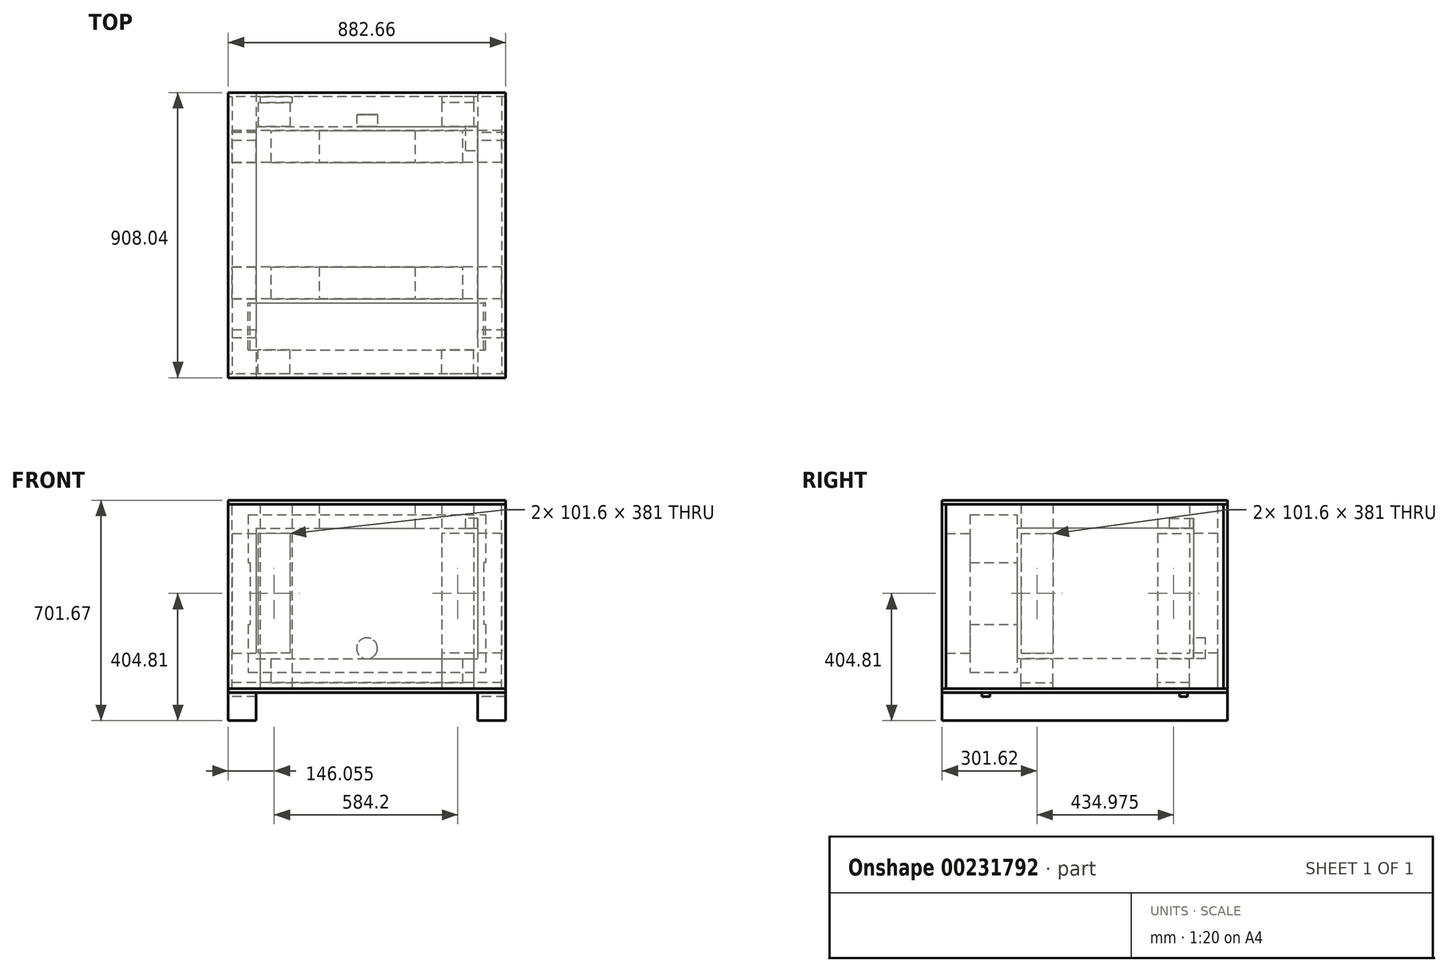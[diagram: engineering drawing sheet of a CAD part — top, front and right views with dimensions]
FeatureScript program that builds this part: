
annotation { "Feature Type Name" : "Feature", "Feature Type Description" : "" }
export const myFeature = defineFeature(function(context is Context, id is Id, definition is map)
    precondition{}
    {
        {
            var Q0;
            Q0=qCreatedBy(makeId("Front.planeOp"),FACE);
            var sketch = newSketch(context, id + "F0", { "sketchPlane" : qUnion([Q0])});
            skLineSegment(sketch, "E0.bottom", {"start": v(-377.83, 250.83) * mm, "end": v(377.83, 250.82) * mm});
            skLineSegment(sketch, "E0.top", {"start": v(-377.83, -250.82) * mm, "end": v(377.83, -250.83) * mm});
            skLineSegment(sketch, "E0.left", {"start": v(-377.82, 250.82) * mm, "end": v(-377.82, 98.43) * mm});
            skLineSegment(sketch, "E0.right", {"start": v(377.83, 250.83) * mm, "end": v(377.83, 98.43) * mm});
            skLineSegment(sketch, "E1.bottom", {"start": v(-377.82, 98.43) * mm, "end": v(-371.47, 98.43) * mm});
            skLineSegment(sketch, "E1.top", {"start": v(-377.83, -98.42) * mm, "end": v(-371.48, -98.42) * mm});
            skLineSegment(sketch, "E1.right", {"start": v(-371.48, 98.43) * mm, "end": v(-371.48, -98.42) * mm});
            skLineSegment(sketch, "E2", {"start": v(0, 250.82) * mm, "end": v(0, -250.82) * mm, "construction": true});
            skLineSegment(sketch, "E3.MirrorCS", {"start": v(377.82, 98.42) * mm, "end": v(371.47, 98.42) * mm});
            skLineSegment(sketch, "E4.MirrorCS", {"start": v(377.83, -98.43) * mm, "end": v(371.48, -98.43) * mm});
            skLineSegment(sketch, "E5.MirrorCS", {"start": v(371.47, 98.43) * mm, "end": v(371.48, -98.42) * mm});
            skLineSegment(sketch, "E6.trimOffspring", {"start": v(377.83, -98.42) * mm, "end": v(377.82, -250.83) * mm});
            skLineSegment(sketch, "E7.trimOffspring", {"start": v(-377.83, -98.42) * mm, "end": v(-377.83, -250.82) * mm});
            skLineSegment(sketch, "E8", {"start": v(371.48, 0) * mm, "end": v(-371.48, 0) * mm, "construction": true});
            skPoint(sketch, "E9", {"position": v(0, 0) * mm});
            skPoint(sketch, "E9.positionSnap0", {"position": v(0, 0) * mm});
            skSolve(sketch);
        }
        {
            var Q0;
            Q0=qSketchRegion(id+"F0",true);
            extrude(context, id + "F1", {"entities" : qUnion([Q0]), "depth" : 149.22 * mm});
        }
        {
            var Q0;
            Q0=makeQuery(id+"F1.opExtrude","CAP_FACE",FACE,{"disambiguationData":[OSD([sQuery(id+"F0.wireOp",EDGE,"E0.bottom"),sQuery(id+"F0.wireOp",EDGE,"E0.top"),sQuery(id+"F0.wireOp",EDGE,"E0.left"),sQuery(id+"F0.wireOp",EDGE,"E1.bottom"),sQuery(id+"F0.wireOp",EDGE,"E1.top"),sQuery(id+"F0.wireOp",EDGE,"E1.right"),sQuery(id+"F0.wireOp",EDGE,"E3.MirrorCS"),sQuery(id+"F0.wireOp",EDGE,"E4.MirrorCS"),sQuery(id+"F0.wireOp",EDGE,"E5.MirrorCS"),sQuery(id+"F0.wireOp",EDGE,"E0.right"),sQuery(id+"F0.wireOp",EDGE,"E7.trimOffspring"),sQuery(id+"F0.wireOp",EDGE,"E6.trimOffspring")])],"isStart":true});
            var sketch = newSketch(context, id + "F2", { "sketchPlane" : qUnion([Q0])});
            skPoint(sketch, "E10.0", {"position": v(377.82, 250.82) * mm});
            skPoint(sketch, "E11.0", {"position": v(-377.83, 250.83) * mm});
            skPoint(sketch, "E12.0", {"position": v(377.83, -250.82) * mm});
            skPoint(sketch, "E13.0", {"position": v(-377.82, -250.83) * mm});
            skLineSegment(sketch, "E14.bottom", {"start": v(352.43, 207.96) * mm, "end": v(-352.43, 207.96) * mm});
            skLineSegment(sketch, "E14.top", {"start": v(352.43, -207.96) * mm, "end": v(-352.43, -207.96) * mm});
            skLineSegment(sketch, "E14.left", {"start": v(352.43, 207.96) * mm, "end": v(352.43, -207.96) * mm});
            skLineSegment(sketch, "E14.right", {"start": v(-352.43, 207.96) * mm, "end": v(-352.43, -207.96) * mm});
            skPoint(sketch, "E14.middle", {"position": v(0, 0) * mm});
            skSolve(sketch);
        }
        {
            var Q0;
            Q0=qSketchRegion(id+"F2",true);
            extrude(context, id + "F3", {"entities" : qUnion([Q0]), "operationType" : NewBodyOperationType.ADD, "depth" : 561.98 * mm});
        }
        {
            var Q0;
            Q0=makeQuery(id+"F3.opExtrude","CAP_FACE",FACE,{"disambiguationData":[OSD([sQuery(id+"F2.wireOp",EDGE,"E14.bottom"),sQuery(id+"F2.wireOp",EDGE,"E14.top"),sQuery(id+"F2.wireOp",EDGE,"E14.left"),sQuery(id+"F2.wireOp",EDGE,"E14.right")])],"isStart":false});
            var sketch = newSketch(context, id + "F4", { "sketchPlane" : qUnion([Q0])});
            skLineSegment(sketch, "E15.bottom", {"start": v(-352.43, 207.96) * mm, "end": v(-314.33, 207.96) * mm});
            skLineSegment(sketch, "E15.top", {"start": v(-352.43, 239.71) * mm, "end": v(-314.33, 239.71) * mm});
            skLineSegment(sketch, "E15.left", {"start": v(-352.43, 207.96) * mm, "end": v(-352.43, 239.71) * mm});
            skLineSegment(sketch, "E15.right", {"start": v(-314.33, 207.96) * mm, "end": v(-314.33, 239.71) * mm});
            skSolve(sketch);
        }
        {
            var Q0;
            Q0=qSketchRegion(id+"F4",true);
            extrude(context, id + "F5", {"entities" : qUnion([Q0]), "operationType" : NewBodyOperationType.ADD, "oppositeDirection" : true, "depth" : 76.2 * mm});
        }
        {
            var Q0;
            Q0=makeQuery(id+"F5.boolean.opBoolean","MERGE",FACE,{"derivedFrom":[makeQuery(id+"F3.opExtrude","CAP_FACE",FACE,{"disambiguationData":[OSD([sQuery(id+"F2.wireOp",EDGE,"E14.bottom"),sQuery(id+"F2.wireOp",EDGE,"E14.top"),sQuery(id+"F2.wireOp",EDGE,"E14.left"),sQuery(id+"F2.wireOp",EDGE,"E14.right")])],"isStart":false}),makeQuery(id+"F5.opExtrude","CAP_FACE",FACE,{"disambiguationData":[OSD([sQuery(id+"F4.wireOp",EDGE,"E15.bottom"),sQuery(id+"F4.wireOp",EDGE,"E15.top"),sQuery(id+"F4.wireOp",EDGE,"E15.left"),sQuery(id+"F4.wireOp",EDGE,"E15.right")])],"isStart":true})]});
            var sketch = newSketch(context, id + "F6", { "sketchPlane" : qUnion([Q0])});
            skLineSegment(sketch, "E16", {"start": v(0, -207.96) * mm, "end": v(0, -174.63) * mm, "construction": true});
            skPoint(sketch, "E16.endSnap0", {"position": v(0, -207.96) * mm});
            skCircle(sketch, "E17", {"center": v(0, -174.63) * mm, "radius": 33.34 * mm});
            skSolve(sketch);
        }
        {
            var Q0;
            Q0=qSketchRegion(id+"F6",true);
            var Q1;
            Q1=qConstructionFilter(qBodyType(qCreatedBy(id+"F6",EDGE),BodyType.WIRE),ConstructionObject.NO);
            extrude(context, id + "F7", {"entities" : qUnion([Q0]), "operationType" : NewBodyOperationType.ADD, "surfaceEntities" : qUnion([Q1]), "depth" : 38.1 * mm});
        }
        {
            var Q0;
            Q0=makeQuery(id+"F3.opExtrude","SWEPT_FACE",FACE,{"disambiguationData":[OSD([sQuery(id+"F2.wireOp",EDGE,"E14.top")])]});
            var sketch = newSketch(context, id + "F8", { "sketchPlane" : qUnion([Q0])});
            skLineSegment(sketch, "E18.bottom", {"start": v(-304.8, -12.7) * mm, "end": v(304.8, -12.7) * mm});
            skLineSegment(sketch, "E18.top", {"start": v(-304.8, -114.3) * mm, "end": v(304.8, -114.3) * mm});
            skLineSegment(sketch, "E18.left", {"start": v(-304.8, -12.7) * mm, "end": v(-304.8, -114.3) * mm});
            skLineSegment(sketch, "E18.right", {"start": v(304.8, -12.7) * mm, "end": v(304.8, -114.3) * mm});
            skLineSegment(sketch, "E19.bottom", {"start": v(-304.8, -447.67) * mm, "end": v(304.8, -447.67) * mm});
            skLineSegment(sketch, "E19.top", {"start": v(-304.8, -549.27) * mm, "end": v(304.8, -549.27) * mm});
            skLineSegment(sketch, "E19.left", {"start": v(-304.8, -447.67) * mm, "end": v(-304.8, -549.27) * mm});
            skLineSegment(sketch, "E19.right", {"start": v(304.8, -447.67) * mm, "end": v(304.8, -549.27) * mm});
            skLineSegment(sketch, "E20", {"start": v(0, 0) * mm, "end": v(0, -561.98) * mm, "construction": true});
            skPoint(sketch, "E21", {"position": v(0, -114.3) * mm});
            skPoint(sketch, "E22", {"position": v(0, -447.67) * mm});
            skLineSegment(sketch, "E23.0", {"start": v(-377.83, 0) * mm, "end": v(377.82, 0) * mm, "construction": true});
            skLineSegment(sketch, "E24.0", {"start": v(0, -561.98) * mm, "end": v(352.43, -561.98) * mm, "construction": true});
            skLineSegment(sketch, "E25.0", {"start": v(-352.43, -561.98) * mm, "end": v(0, -561.98) * mm, "construction": true});
            skSolve(sketch);
        }
        {
            var Q0;
            Q0=qSketchRegion(id+"F8",true);
            extrude(context, id + "F9", {"entities" : qUnion([Q0]), "depth" : 76.2 * mm});
        }
        {
            var Q0;
            Q0=makeQuery(id+"F3.opExtrude","SWEPT_FACE",FACE,{"disambiguationData":[OSD([sQuery(id+"F2.wireOp",EDGE,"E14.bottom")])]});
            var sketch = newSketch(context, id + "F10", { "sketchPlane" : qUnion([Q0])});
            skLineSegment(sketch, "E26.0", {"start": v(-352.43, 561.98) * mm, "end": v(314.33, 561.98) * mm, "construction": true});
            skLineSegment(sketch, "E27.0", {"start": v(-377.82, 0) * mm, "end": v(377.83, 0) * mm, "construction": true});
            skPoint(sketch, "E28", {"position": v(0, 0) * mm});
            skLineSegment(sketch, "E29", {"start": v(0, 0) * mm, "end": v(0, 561.98) * mm, "construction": true});
            skLineSegment(sketch, "E30.bottom", {"start": v(-152.4, 549.27) * mm, "end": v(152.4, 549.27) * mm});
            skLineSegment(sketch, "E30.top", {"start": v(-152.4, 447.67) * mm, "end": v(152.4, 447.67) * mm});
            skLineSegment(sketch, "E30.left", {"start": v(-152.4, 549.27) * mm, "end": v(-152.4, 447.67) * mm});
            skLineSegment(sketch, "E30.right", {"start": v(152.4, 549.27) * mm, "end": v(152.4, 447.67) * mm});
            skLineSegment(sketch, "E31.bottom", {"start": v(-152.4, 114.3) * mm, "end": v(152.4, 114.3) * mm});
            skLineSegment(sketch, "E31.top", {"start": v(-152.4, 12.7) * mm, "end": v(152.4, 12.7) * mm});
            skLineSegment(sketch, "E31.left", {"start": v(-152.4, 114.3) * mm, "end": v(-152.4, 12.7) * mm});
            skLineSegment(sketch, "E31.right", {"start": v(152.4, 114.3) * mm, "end": v(152.4, 12.7) * mm});
            skPoint(sketch, "E32", {"position": v(0, 549.27) * mm});
            skPoint(sketch, "E33", {"position": v(0, 114.3) * mm});
            skSolve(sketch);
        }
        {
            var Q0;
            Q0=qSketchRegion(id+"F10",true);
            extrude(context, id + "F11", {"entities" : qUnion([Q0]), "depth" : 76.2 * mm});
        }
        {
            var Q0;
            Q0=makeQuery(id+"F5.boolean.opBoolean","MERGE",FACE,{"derivedFrom":[makeQuery(id+"F3.opExtrude","SWEPT_FACE",FACE,{"disambiguationData":[OSD([sQuery(id+"F2.wireOp",EDGE,"E14.right")])]}),makeQuery(id+"F5.opExtrude","SWEPT_FACE",FACE,{"disambiguationData":[OSD([sQuery(id+"F4.wireOp",EDGE,"E15.left")])]})]});
            var sketch = newSketch(context, id + "F12", { "sketchPlane" : qUnion([Q0])});
            skLineSegment(sketch, "E34.bottom", {"start": v(12.7, 190.5) * mm, "end": v(114.3, 190.5) * mm});
            skLineSegment(sketch, "E34.top", {"start": v(12.7, -190.5) * mm, "end": v(114.3, -190.5) * mm});
            skLineSegment(sketch, "E34.left", {"start": v(12.7, 190.5) * mm, "end": v(12.7, -190.5) * mm});
            skLineSegment(sketch, "E34.right", {"start": v(114.3, 190.5) * mm, "end": v(114.3, -190.5) * mm});
            skLineSegment(sketch, "E35.bottom", {"start": v(447.67, 190.5) * mm, "end": v(549.27, 190.5) * mm});
            skLineSegment(sketch, "E35.top", {"start": v(447.67, -190.5) * mm, "end": v(549.27, -190.5) * mm});
            skLineSegment(sketch, "E35.left", {"start": v(447.67, 190.5) * mm, "end": v(447.67, -190.5) * mm});
            skLineSegment(sketch, "E35.right", {"start": v(549.27, 190.5) * mm, "end": v(549.27, -190.5) * mm});
            skPoint(sketch, "E36", {"position": v(549.27, 0) * mm});
            skLineSegment(sketch, "E37.0", {"start": v(561.98, 207.96) * mm, "end": v(561.98, -207.96) * mm, "construction": true});
            skPoint(sketch, "E38", {"position": v(561.98, 0) * mm});
            skLineSegment(sketch, "E39", {"start": v(561.98, 0) * mm, "end": v(-342.54, 0) * mm, "construction": true});
            skSolve(sketch);
        }
        {
            var Q0;
            Q0=qSketchRegion(id+"F12",true);
            extrude(context, id + "F13", {"entities" : qUnion([Q0]), "depth" : 76.2 * mm});
        }
        {
            var Q0;
            Q0=makeQuery(id+"F9.opExtrude","CAP_FACE",FACE,{"disambiguationData":[OSD([sQuery(id+"F8.wireOp",EDGE,"E18.bottom"),sQuery(id+"F8.wireOp",EDGE,"E18.top"),sQuery(id+"F8.wireOp",EDGE,"E18.left"),sQuery(id+"F8.wireOp",EDGE,"E18.right")])],"isStart":false});
            var sketch = newSketch(context, id + "F14", { "sketchPlane" : qUnion([Q0])});
            skPoint(sketch, "E40.0", {"position": v(428.63, -12.7) * mm});
            skLineSegment(sketch, "E41.bottom", {"start": v(428.63, -12.7) * mm, "end": v(-428.63, -12.7) * mm});
            skLineSegment(sketch, "E41.top", {"start": v(428.63, -114.3) * mm, "end": v(-428.63, -114.3) * mm});
            skLineSegment(sketch, "E41.left", {"start": v(428.63, -12.7) * mm, "end": v(428.63, -114.3) * mm});
            skLineSegment(sketch, "E41.right", {"start": v(-428.63, -12.7) * mm, "end": v(-428.63, -114.3) * mm});
            skPoint(sketch, "E42.0", {"position": v(428.63, -549.27) * mm});
            skLineSegment(sketch, "E43.bottom", {"start": v(428.63, -549.27) * mm, "end": v(-428.63, -549.27) * mm});
            skLineSegment(sketch, "E43.top", {"start": v(428.63, -447.67) * mm, "end": v(-428.63, -447.68) * mm});
            skLineSegment(sketch, "E43.left", {"start": v(428.63, -549.27) * mm, "end": v(428.63, -447.67) * mm});
            skLineSegment(sketch, "E43.right", {"start": v(-428.63, -549.28) * mm, "end": v(-428.63, -447.68) * mm});
            skPoint(sketch, "E44.0", {"position": v(0, -447.67) * mm});
            skSolve(sketch);
        }
        {
            var Q0;
            Q0=qSketchRegion(id+"F14",true);
            extrude(context, id + "F15", {"entities" : qUnion([Q0]), "depth" : 19.05 * mm});
        }
        {
            var Q0;
            Q0=makeQuery(id+"F5.boolean.opBoolean","MERGE",FACE,{"derivedFrom":[makeQuery(id+"F3.opExtrude","CAP_FACE",FACE,{"disambiguationData":[OSD([sQuery(id+"F2.wireOp",EDGE,"E14.bottom"),sQuery(id+"F2.wireOp",EDGE,"E14.top"),sQuery(id+"F2.wireOp",EDGE,"E14.left"),sQuery(id+"F2.wireOp",EDGE,"E14.right")])],"isStart":false}),makeQuery(id+"F5.opExtrude","CAP_FACE",FACE,{"disambiguationData":[OSD([sQuery(id+"F4.wireOp",EDGE,"E15.bottom"),sQuery(id+"F4.wireOp",EDGE,"E15.top"),sQuery(id+"F4.wireOp",EDGE,"E15.left"),sQuery(id+"F4.wireOp",EDGE,"E15.right")])],"isStart":true})]});
            var sketch = newSketch(context, id + "F16", { "sketchPlane" : qUnion([Q0])});
            skLineSegment(sketch, "E45.0", {"start": v(0, -207.96) * mm, "end": v(-352.43, -207.96) * mm, "construction": true});
            skLineSegment(sketch, "E46.0", {"start": v(352.43, -207.96) * mm, "end": v(0, -207.96) * mm, "construction": true});
            skLineSegment(sketch, "E47.0", {"start": v(352.43, 207.96) * mm, "end": v(352.43, -207.96) * mm, "construction": true});
            skLineSegment(sketch, "E48.bottom", {"start": v(-339.73, 190.5) * mm, "end": v(-238.12, 190.5) * mm});
            skLineSegment(sketch, "E48.top", {"start": v(-339.73, -190.5) * mm, "end": v(-238.12, -190.5) * mm});
            skLineSegment(sketch, "E48.left", {"start": v(-339.73, 190.5) * mm, "end": v(-339.73, -190.5) * mm});
            skLineSegment(sketch, "E48.right", {"start": v(-238.13, 190.5) * mm, "end": v(-238.13, -190.5) * mm});
            skLineSegment(sketch, "E49.bottom", {"start": v(244.47, 190.5) * mm, "end": v(346.08, 190.5) * mm});
            skLineSegment(sketch, "E49.top", {"start": v(244.47, -190.5) * mm, "end": v(346.08, -190.5) * mm});
            skLineSegment(sketch, "E49.left", {"start": v(244.47, 190.5) * mm, "end": v(244.47, -190.5) * mm});
            skLineSegment(sketch, "E49.right", {"start": v(346.08, 190.5) * mm, "end": v(346.08, -190.5) * mm});
            skPoint(sketch, "E50", {"position": v(352.43, 0) * mm});
            skLineSegment(sketch, "E51", {"start": v(352.43, 0) * mm, "end": v(-564.26, 0) * mm, "construction": true});
            skPoint(sketch, "E52", {"position": v(346.08, 0) * mm});
            skSolve(sketch);
        }
        {
            var Q0;
            Q0=qSketchRegion(id+"F16",true);
            extrude(context, id + "F17", {"entities" : qUnion([Q0]), "depth" : 76.2 * mm});
        }
        {
            var Q0;
            Q0=makeQuery(id+"F3.opExtrude","SWEPT_FACE",FACE,{"disambiguationData":[OSD([sQuery(id+"F2.wireOp",EDGE,"E14.left")])]});
            cPlane(context, id + "F18", {"entities" : qUnion([Q0]), "cplaneType" : CPlaneType.OFFSET, "offset" : 352.42 * mm, "oppositeDirection" : true, "width" : 152.4 * mm, "height" : 152.4 * mm});
        }
        {
            var Q0;
            Q0=makeQuery(id+"F13.opExtrude","SWEPT_BODY",BODY,{"disambiguationData":[OSD([sQuery(id+"F12.wireOp",EDGE,"E35.bottom"),sQuery(id+"F12.wireOp",EDGE,"E35.top"),sQuery(id+"F12.wireOp",EDGE,"E35.left"),sQuery(id+"F12.wireOp",EDGE,"E35.right")])]});
            var Q1;
            Q1=makeQuery(id+"F13.opExtrude","SWEPT_BODY",BODY,{"disambiguationData":[OSD([sQuery(id+"F12.wireOp",EDGE,"E34.bottom"),sQuery(id+"F12.wireOp",EDGE,"E34.top"),sQuery(id+"F12.wireOp",EDGE,"E34.left"),sQuery(id+"F12.wireOp",EDGE,"E34.right")])]});
            var Q2;
            Q2=qCreatedBy(id+"F18.planeOp",FACE);
            mirror(context, id + "F19", {"operationType" : NewBodyOperationType.ADD, "entities" : qUnion([Q0, Q1]), "mirrorPlane" : qUnion([Q2])});
        }
        {
            var Q0;
            Q0=makeQuery(id+"F1.opExtrude","CAP_FACE",FACE,{"disambiguationData":[OSD([sQuery(id+"F0.wireOp",EDGE,"E0.bottom"),sQuery(id+"F0.wireOp",EDGE,"E0.top"),sQuery(id+"F0.wireOp",EDGE,"E0.left"),sQuery(id+"F0.wireOp",EDGE,"E1.bottom"),sQuery(id+"F0.wireOp",EDGE,"E1.top"),sQuery(id+"F0.wireOp",EDGE,"E1.right"),sQuery(id+"F0.wireOp",EDGE,"E3.MirrorCS"),sQuery(id+"F0.wireOp",EDGE,"E4.MirrorCS"),sQuery(id+"F0.wireOp",EDGE,"E5.MirrorCS"),sQuery(id+"F0.wireOp",EDGE,"E0.right"),sQuery(id+"F0.wireOp",EDGE,"E7.trimOffspring"),sQuery(id+"F0.wireOp",EDGE,"E6.trimOffspring")])],"isStart":false});
            cPlane(context, id + "F20", {"entities" : qUnion([Q0]), "cplaneType" : CPlaneType.OFFSET, "offset" : 355.6 * mm, "oppositeDirection" : true, "width" : 152.4 * mm, "height" : 152.4 * mm});
        }
        {
            var Q0;
            Q0=makeQuery(id+"F17.opExtrude","SWEPT_BODY",BODY,{"disambiguationData":[OSD([sQuery(id+"F16.wireOp",EDGE,"E49.bottom"),sQuery(id+"F16.wireOp",EDGE,"E49.top"),sQuery(id+"F16.wireOp",EDGE,"E49.left"),sQuery(id+"F16.wireOp",EDGE,"E49.right")])]});
            var Q1;
            Q1=makeQuery(id+"F17.opExtrude","SWEPT_BODY",BODY,{"disambiguationData":[OSD([sQuery(id+"F16.wireOp",EDGE,"E48.bottom"),sQuery(id+"F16.wireOp",EDGE,"E48.top"),sQuery(id+"F16.wireOp",EDGE,"E48.left"),sQuery(id+"F16.wireOp",EDGE,"E48.right")])]});
            var Q2;
            Q2=qCreatedBy(id+"F20.planeOp",FACE);
            mirror(context, id + "F21", {"operationType" : NewBodyOperationType.ADD, "entities" : qUnion([Q0, Q1]), "mirrorPlane" : qUnion([Q2])});
        }
        {
            var Q0;
            Q0=makeQuery(id+"F17.opExtrude","CAP_FACE",FACE,{"disambiguationData":[OSD([sQuery(id+"F16.wireOp",EDGE,"E48.bottom"),sQuery(id+"F16.wireOp",EDGE,"E48.top"),sQuery(id+"F16.wireOp",EDGE,"E48.left"),sQuery(id+"F16.wireOp",EDGE,"E48.right")])],"isStart":false});
            var sketch = newSketch(context, id + "F22", { "sketchPlane" : qUnion([Q0])});
            skLineSegment(sketch, "E53.bottom", {"start": v(-339.73, 284.16) * mm, "end": v(-238.13, 284.16) * mm});
            skLineSegment(sketch, "E53.top", {"start": v(-339.73, -303.21) * mm, "end": v(-238.12, -303.21) * mm});
            skLineSegment(sketch, "E53.left", {"start": v(-339.73, 284.16) * mm, "end": v(-339.73, -303.21) * mm});
            skLineSegment(sketch, "E53.right", {"start": v(-238.13, 284.16) * mm, "end": v(-238.13, -303.21) * mm});
            skLineSegment(sketch, "E54.0", {"start": v(152.4, 284.16) * mm, "end": v(-152.4, 284.16) * mm, "construction": true});
            skLineSegment(sketch, "E55.0", {"start": v(-428.63, -303.21) * mm, "end": v(428.63, -303.21) * mm, "construction": true});
            skSolve(sketch);
        }
        {
            var Q0;
            Q0=qSketchRegion(id+"F22",true);
            extrude(context, id + "F23", {"entities" : qUnion([Q0]), "depth" : 19.05 * mm});
        }
        {
            var Q0;
            Q0=makeQuery(id+"F23.opExtrude","SWEPT_BODY",BODY,{"disambiguationData":[OSD([sQuery(id+"F22.wireOp",EDGE,"E53.bottom"),sQuery(id+"F22.wireOp",EDGE,"E53.top"),sQuery(id+"F22.wireOp",EDGE,"E53.left"),sQuery(id+"F22.wireOp",EDGE,"E53.right")])]});
            var Q1;
            Q1=qCreatedBy(id+"F18.planeOp",FACE);
            mirror(context, id + "F24", {"operationType" : NewBodyOperationType.ADD, "entities" : qUnion([Q0]), "mirrorPlane" : qUnion([Q1])});
        }
        {
            var Q0;
            Q0=makeQuery(id+"F15.opExtrude","CAP_FACE",FACE,{"disambiguationData":[OSD([sQuery(id+"F14.wireOp",EDGE,"E41.bottom"),sQuery(id+"F14.wireOp",EDGE,"E41.top"),sQuery(id+"F14.wireOp",EDGE,"E41.left"),sQuery(id+"F14.wireOp",EDGE,"E41.right")])],"isStart":false});
            var sketch = newSketch(context, id + "F25", { "sketchPlane" : qUnion([Q0])});
            skPoint(sketch, "E56.0", {"position": v(339.73, -657.23) * mm});
            skPoint(sketch, "E57.0", {"position": v(428.63, -549.27) * mm});
            skPoint(sketch, "E58.0", {"position": v(339.73, 225.43) * mm});
            skPoint(sketch, "E59.0", {"position": v(-428.63, -12.7) * mm});
            skLineSegment(sketch, "E60.bottom", {"start": v(441.33, -669.93) * mm, "end": v(-441.33, -669.93) * mm});
            skLineSegment(sketch, "E60.top", {"start": v(441.32, 238.13) * mm, "end": v(-441.33, 238.12) * mm});
            skLineSegment(sketch, "E60.left", {"start": v(441.33, -669.93) * mm, "end": v(441.32, 238.13) * mm});
            skLineSegment(sketch, "E60.right", {"start": v(-441.33, -669.93) * mm, "end": v(-441.33, 238.12) * mm});
            skSolve(sketch);
        }
        {
            var Q0;
            Q0=qSketchRegion(id+"F25",true);
            extrude(context, id + "F26", {"entities" : qUnion([Q0]), "depth" : 12.7 * mm});
        }
        {
            var Q0;
            Q0=makeQuery(id+"F13.opExtrude","CAP_FACE",FACE,{"disambiguationData":[OSD([sQuery(id+"F12.wireOp",EDGE,"E35.bottom"),sQuery(id+"F12.wireOp",EDGE,"E35.top"),sQuery(id+"F12.wireOp",EDGE,"E35.left"),sQuery(id+"F12.wireOp",EDGE,"E35.right")])],"isStart":false});
            var sketch = newSketch(context, id + "F27", { "sketchPlane" : qUnion([Q0])});
            skPoint(sketch, "E61.0", {"position": v(657.23, -303.21) * mm});
            skLineSegment(sketch, "E62.0", {"start": v(-225.43, 190.5) * mm, "end": v(-225.43, -190.5) * mm, "construction": true});
            skLineSegment(sketch, "E63.bottom", {"start": v(657.23, -303.21) * mm, "end": v(-225.42, -303.21) * mm});
            skLineSegment(sketch, "E63.top", {"start": v(657.22, 284.16) * mm, "end": v(-225.43, 284.16) * mm});
            skLineSegment(sketch, "E63.left", {"start": v(657.23, -303.21) * mm, "end": v(657.23, 284.16) * mm});
            skLineSegment(sketch, "E63.right", {"start": v(-225.42, -303.21) * mm, "end": v(-225.43, 284.16) * mm});
            skPoint(sketch, "E64.0", {"position": v(549.27, 284.16) * mm});
            skSolve(sketch);
        }
        {
            var Q0;
            Q0=qSketchRegion(id+"F27",true);
            extrude(context, id + "F28", {"entities" : qUnion([Q0]), "depth" : 12.7 * mm});
        }
        {
            var Q0;
            Q0=makeQuery(id+"F28.opExtrude","SWEPT_BODY",BODY,{"disambiguationData":[OSD([sQuery(id+"F27.wireOp",EDGE,"E63.bottom"),sQuery(id+"F27.wireOp",EDGE,"E63.top"),sQuery(id+"F27.wireOp",EDGE,"E63.left"),sQuery(id+"F27.wireOp",EDGE,"E63.right")])]});
            var Q1;
            Q1=qCreatedBy(id+"F18.planeOp",FACE);
            mirror(context, id + "F29", {"entities" : qUnion([Q0]), "mirrorPlane" : qUnion([Q1])});
        }
        {
            var Q0;
            Q0=makeQuery(id+"F23.opExtrude","CAP_FACE",FACE,{"disambiguationData":[OSD([sQuery(id+"F22.wireOp",EDGE,"E53.bottom"),sQuery(id+"F22.wireOp",EDGE,"E53.top"),sQuery(id+"F22.wireOp",EDGE,"E53.left"),sQuery(id+"F22.wireOp",EDGE,"E53.right")])],"isStart":false});
            var sketch = newSketch(context, id + "F30", { "sketchPlane" : qUnion([Q0])});
            skLineSegment(sketch, "E65.0", {"start": v(-441.33, -303.21) * mm, "end": v(-441.33, 284.16) * mm});
            skLineSegment(sketch, "E66.0", {"start": v(-441.33, -303.21) * mm, "end": v(441.33, -303.21) * mm});
            skLineSegment(sketch, "E67.0", {"start": v(441.33, -303.21) * mm, "end": v(441.33, 284.16) * mm});
            skLineSegment(sketch, "E68", {"start": v(-441.33, 284.16) * mm, "end": v(441.33, 284.16) * mm});
            skSolve(sketch);
        }
        {
            var Q0;
            Q0=qSketchRegion(id+"F30",true);
            extrude(context, id + "F31", {"entities" : qUnion([Q0]), "depth" : 12.7 * mm});
        }
        {
            var Q0;
            Q0=makeQuery(id+"F21.opPattern","COPY",FACE,{"derivedFrom":makeQuery(id+"F17.opExtrude","CAP_FACE",FACE,{"disambiguationData":[OSD([sQuery(id+"F16.wireOp",EDGE,"E48.bottom"),sQuery(id+"F16.wireOp",EDGE,"E48.top"),sQuery(id+"F16.wireOp",EDGE,"E48.left"),sQuery(id+"F16.wireOp",EDGE,"E48.right")])],"isStart":false}),"instanceName":"1"});
            var sketch = newSketch(context, id + "F32", { "sketchPlane" : qUnion([Q0])});
            skLineSegment(sketch, "E69.0", {"start": v(-441.33, -303.21) * mm, "end": v(-441.33, 284.16) * mm});
            skLineSegment(sketch, "E70.0", {"start": v(441.33, -303.21) * mm, "end": v(441.33, 284.16) * mm});
            skLineSegment(sketch, "E71.0", {"start": v(441.32, -303.21) * mm, "end": v(-441.33, -303.21) * mm});
            skLineSegment(sketch, "E72", {"start": v(-441.33, 284.16) * mm, "end": v(441.33, 284.16) * mm});
            skSolve(sketch);
        }
        {
            var Q0;
            Q0=qSketchRegion(id+"F32",true);
            extrude(context, id + "F33", {"entities" : qUnion([Q0]), "depth" : 12.7 * mm});
        }
        {
            var Q0;
            Q0=makeQuery(id+"F11.opExtrude","CAP_FACE",FACE,{"disambiguationData":[OSD([sQuery(id+"F10.wireOp",EDGE,"E31.bottom"),sQuery(id+"F10.wireOp",EDGE,"E31.top"),sQuery(id+"F10.wireOp",EDGE,"E31.left"),sQuery(id+"F10.wireOp",EDGE,"E31.right")])],"isStart":false});
            var sketch = newSketch(context, id + "F34", { "sketchPlane" : qUnion([Q0])});
            skPoint(sketch, "E73.0", {"position": v(-441.33, 669.93) * mm});
            skPoint(sketch, "E74.0", {"position": v(441.33, -238.13) * mm});
            skLineSegment(sketch, "E75.bottom", {"start": v(-441.33, 669.93) * mm, "end": v(441.33, 669.93) * mm});
            skLineSegment(sketch, "E75.top", {"start": v(-441.33, -238.13) * mm, "end": v(441.33, -238.13) * mm});
            skLineSegment(sketch, "E75.left", {"start": v(-441.33, 669.93) * mm, "end": v(-441.33, -238.13) * mm});
            skLineSegment(sketch, "E75.right", {"start": v(441.33, 669.93) * mm, "end": v(441.33, -238.13) * mm});
            skSolve(sketch);
        }
        {
            var Q0;
            Q0=qSketchRegion(id+"F34",true);
            extrude(context, id + "F35", {"entities" : qUnion([Q0]), "depth" : 12.7 * mm});
        }
        {
            var Q0;
            Q0=makeQuery(id+"F26.opExtrude","SWEPT_FACE",FACE,{"disambiguationData":[OSD([sQuery(id+"F25.wireOp",EDGE,"E60.top")])]});
            var sketch = newSketch(context, id + "F36", { "sketchPlane" : qUnion([Q0])});
            skLineSegment(sketch, "E76.bottom", {"start": v(-441.33, -315.91) * mm, "end": v(-352.43, -315.91) * mm});
            skLineSegment(sketch, "E76.top", {"start": v(-441.33, -404.81) * mm, "end": v(-352.43, -404.81) * mm});
            skLineSegment(sketch, "E76.left", {"start": v(-441.33, -315.91) * mm, "end": v(-441.33, -404.81) * mm});
            skLineSegment(sketch, "E76.right", {"start": v(-352.43, -315.91) * mm, "end": v(-352.43, -404.81) * mm});
            skLineSegment(sketch, "E77.bottom", {"start": v(441.32, -315.91) * mm, "end": v(352.43, -315.91) * mm});
            skLineSegment(sketch, "E77.top", {"start": v(441.32, -404.81) * mm, "end": v(352.43, -404.81) * mm});
            skLineSegment(sketch, "E77.left", {"start": v(441.32, -315.91) * mm, "end": v(441.32, -404.81) * mm});
            skLineSegment(sketch, "E77.right", {"start": v(352.43, -315.91) * mm, "end": v(352.43, -404.81) * mm});
            skSolve(sketch);
        }
        {
            var Q0;
            Q0=qSketchRegion(id+"F36",true);
            var Q1;
            Q1=makeQuery(id+"F31.opExtrude","CAP_FACE",FACE,{"disambiguationData":[OSD([sQuery(id+"F30.wireOp",EDGE,"E65.0"),sQuery(id+"F30.wireOp",EDGE,"E66.0"),sQuery(id+"F30.wireOp",EDGE,"E67.0"),sQuery(id+"F30.wireOp",EDGE,"E68")])],"isStart":false});
            extrude(context, id + "F37", {"entities" : qUnion([Q0]), "endBound" : BoundingType.UP_TO_SURFACE, "oppositeDirection" : true, "endBoundEntityFace" : qUnion([Q1]), "depth" : 25.4 * mm});
        }
        {
            var Q0;
            Q0=makeQuery(id+"F37.opExtrude","SWEPT_FACE",FACE,{"disambiguationData":[OSD([sQuery(id+"F36.wireOp",EDGE,"E76.left")])]});
            var sketch = newSketch(context, id + "F38", { "sketchPlane" : qUnion([Q0])});
            skLineSegment(sketch, "E78.bottom", {"start": v(-542.92, -315.91) * mm, "end": v(-517.52, -315.91) * mm});
            skLineSegment(sketch, "E78.top", {"start": v(-542.92, -328.61) * mm, "end": v(-517.52, -328.61) * mm});
            skLineSegment(sketch, "E78.left", {"start": v(-542.92, -315.91) * mm, "end": v(-542.92, -328.61) * mm});
            skLineSegment(sketch, "E78.right", {"start": v(-517.52, -315.91) * mm, "end": v(-517.52, -328.61) * mm});
            skPoint(sketch, "E79", {"position": v(-215.9, -315.91) * mm});
            skLineSegment(sketch, "E80", {"start": v(-215.9, -315.91) * mm, "end": v(-215.9, -390.45) * mm, "construction": true});
            skLineSegment(sketch, "E81.MirrorCS", {"start": v(111.13, -328.61) * mm, "end": v(85.73, -328.61) * mm});
            skLineSegment(sketch, "E82.MirrorCS", {"start": v(85.73, -315.91) * mm, "end": v(85.73, -328.61) * mm});
            skLineSegment(sketch, "E83.MirrorCS", {"start": v(111.13, -315.91) * mm, "end": v(85.73, -315.91) * mm});
            skLineSegment(sketch, "E84.MirrorCS", {"start": v(111.13, -315.91) * mm, "end": v(111.13, -328.61) * mm});
            skSolve(sketch);
        }
        {
            var Q0;
            Q0=qSketchRegion(id+"F38",true);
            extrude(context, id + "F39", {"entities" : qUnion([Q0]), "operationType" : NewBodyOperationType.REMOVE, "endBound" : BoundingType.THROUGH_ALL, "oppositeDirection" : true, "depth" : 25.4 * mm});
        }
    });
